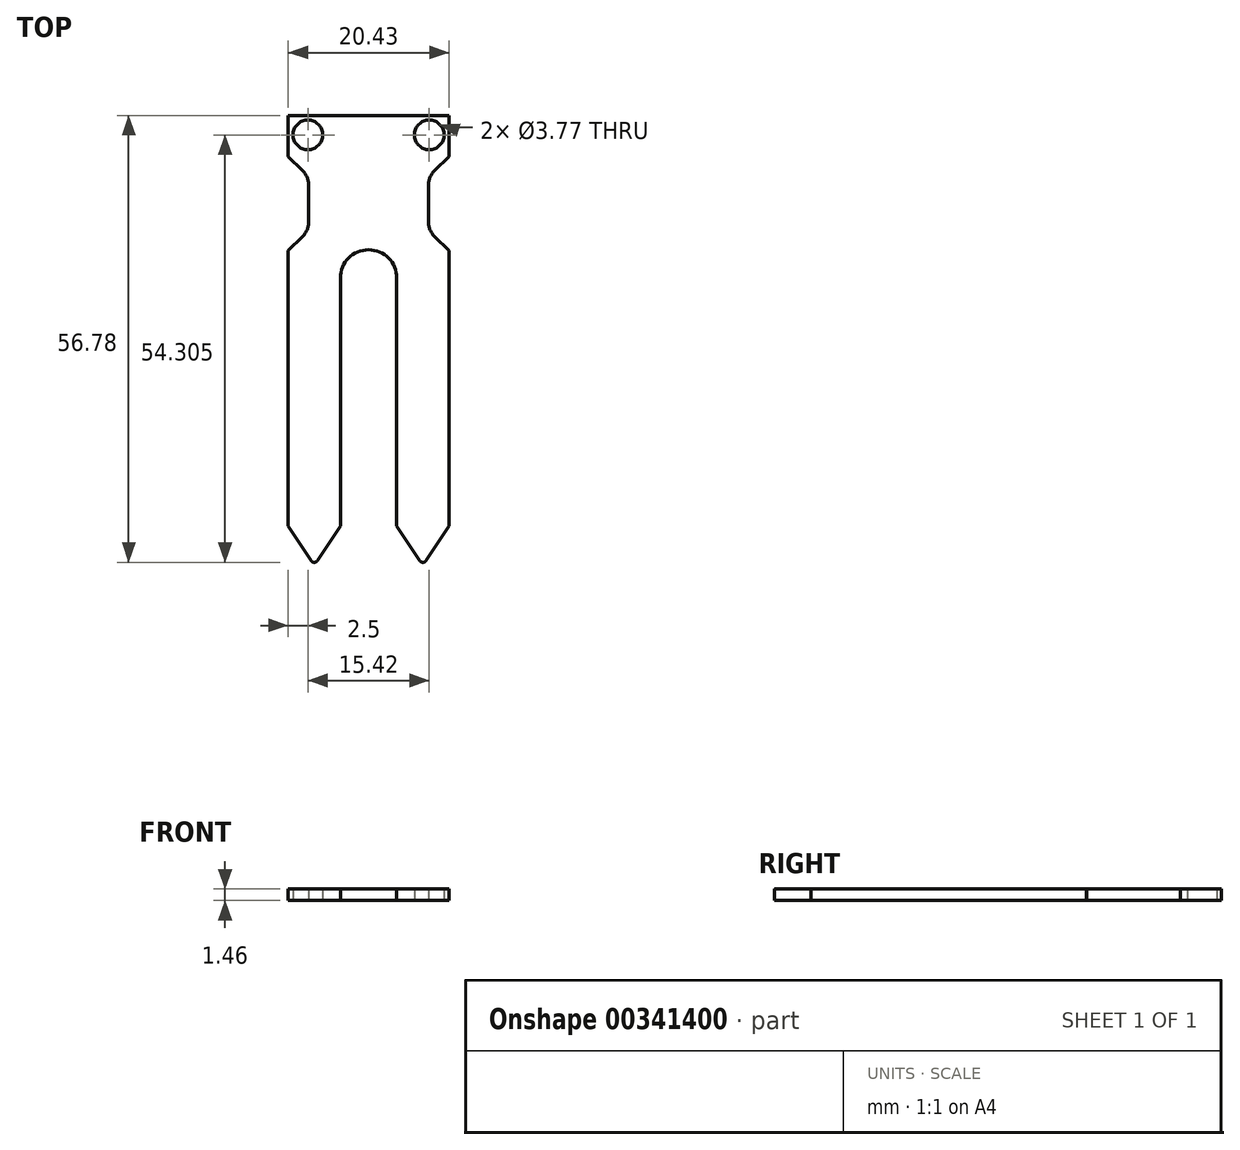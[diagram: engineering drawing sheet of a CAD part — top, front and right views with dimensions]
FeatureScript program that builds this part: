
annotation { "Feature Type Name" : "Feature", "Feature Type Description" : "" }
export const myFeature = defineFeature(function(context is Context, id is Id, definition is map)
    precondition{}
    {
        {
            var Q0;
            Q0=qCreatedBy(makeId("Top.planeOp"),FACE);
            var sketch = newSketch(context, id + "F0", { "sketchPlane" : qUnion([Q0])});
            skPoint(sketch, "E0.middle", {"position": v(0, 0) * mm});
            skLineSegment(sketch, "E1.bottom", {"start": v(-10.21, 10.33) * mm, "end": v(10.22, 10.33) * mm});
            skLineSegment(sketch, "E1.top", {"start": v(-10.22, -10.33) * mm, "end": v(10.21, -10.33) * mm, "construction": true});
            skLineSegment(sketch, "E1.left", {"start": v(-10.21, 10.33) * mm, "end": v(-10.21, -10.33) * mm});
            skLineSegment(sketch, "E1.right", {"start": v(10.21, 10.33) * mm, "end": v(10.21, -10.33) * mm});
            skArc(sketch, "E2", {"start": v(3.58, -10.33) * mm, "mid": v(0, -6.74) * mm, "end": v(-3.59, -10.33) * mm});
            skLineSegment(sketch, "E3", {"start": v(10.21, 10.33) * mm, "end": v(10.21, 5.1) * mm, "construction": true});
            skLineSegment(sketch, "E4", {"start": v(10.21, 5.1) * mm, "end": v(10.21, -6.84) * mm, "construction": true});
            skLineSegment(sketch, "E5", {"start": v(0, 0) * mm, "end": v(0, -25.8) * mm, "construction": true});
            skPoint(sketch, "E5.endSnap0", {"position": v(0, -6.74) * mm});
            skCircle(sketch, "E6", {"center": v(7.7, 7.86) * mm, "radius": 1.89 * mm});
            skCircle(sketch, "E7.MirrorC", {"center": v(-7.7, 7.86) * mm, "radius": 1.89 * mm});
            skLineSegment(sketch, "E8", {"start": v(6.9, -46.86) * mm, "end": v(6.9, -10.33) * mm, "construction": true});
            skPoint(sketch, "E9.oppositeSnap0", {"position": v(10.22, -26.08) * mm});
            skLineSegment(sketch, "E9.bottom", {"start": v(3.58, -10.33) * mm, "end": v(10.22, -10.33) * mm});
            skLineSegment(sketch, "E10", {"start": v(10.21, -10.33) * mm, "end": v(10.21, -41.83) * mm});
            skLineSegment(sketch, "E11", {"start": v(10.21, -41.83) * mm, "end": v(6.9, -46.86) * mm});
            skLineSegment(sketch, "E12.MirrorCS", {"start": v(3.58, -41.83) * mm, "end": v(6.9, -46.86) * mm});
            skLineSegment(sketch, "E13.MirrorCS", {"start": v(3.58, -10.33) * mm, "end": v(3.58, -41.83) * mm});
            skLineSegment(sketch, "E14.MirrorCS", {"start": v(-3.58, -10.33) * mm, "end": v(-3.58, -41.83) * mm});
            skLineSegment(sketch, "E15.MirrorCS", {"start": v(-3.58, -41.83) * mm, "end": v(-6.9, -46.86) * mm});
            skLineSegment(sketch, "E16.MirrorCS", {"start": v(-10.22, -41.83) * mm, "end": v(-6.9, -46.86) * mm});
            skLineSegment(sketch, "E17.MirrorCS", {"start": v(-10.21, -10.33) * mm, "end": v(-10.22, -41.83) * mm});
            skLineSegment(sketch, "E18", {"start": v(10.21, -6.84) * mm, "end": v(10.21, -4.3) * mm, "construction": true});
            skLineSegment(sketch, "E19", {"start": v(10.21, -0.87) * mm, "end": v(6.5, -0.87) * mm, "construction": true});
            skLineSegment(sketch, "E20.MirrorCS", {"start": v(10.22, 5.1) * mm, "end": v(10.22, 2.56) * mm, "construction": true});
            skPoint(sketch, "E21.endSnap0", {"position": v(8.35, -0.87) * mm});
            skLineSegment(sketch, "E22", {"start": v(10.22, 2.56) * mm, "end": v(7.6, 2.56) * mm, "construction": true});
            skLineSegment(sketch, "E23", {"start": v(10.21, 5.1) * mm, "end": v(7.6, 2.56) * mm});
            skLineSegment(sketch, "E24.MirrorCS", {"start": v(10.21, -6.84) * mm, "end": v(7.6, -4.3) * mm});
            skLineSegment(sketch, "E25", {"start": v(7.6, 2.56) * mm, "end": v(7.6, -4.3) * mm});
            skLineSegment(sketch, "E26.MirrorCS", {"start": v(-10.21, 5.1) * mm, "end": v(-7.6, 2.56) * mm});
            skLineSegment(sketch, "E27.MirrorCS", {"start": v(-7.6, 2.56) * mm, "end": v(-7.6, -4.3) * mm});
            skLineSegment(sketch, "E28.MirrorCS", {"start": v(-10.21, -6.84) * mm, "end": v(-7.6, -4.3) * mm});
            skSolve(sketch);
        }
        {
            var Q0;
            Q0=makeQuery(id+"F0.imprint","IMPRINT",FACE,{"disambiguationData":[TD([[makeQuery(id+"F0.imprint","IMPRINT",EDGE,{"derivedFrom":sQuery(id+"F0.wireOp",EDGE,"E1.bottom")}),-1.0]])]});
            var Q1;
            Q1=makeQuery(id+"F0.imprint","IMPRINT",FACE,{"disambiguationData":[TD([[makeQuery(id+"F0.imprint","IMPRINT",EDGE,{"derivedFrom":sQuery(id+"F0.wireOp",EDGE,"E9.bottom")}),-1.0]])]});
            extrude(context, id + "F1", {"entities" : qUnion([Q0, Q1]), "depth" : 1.46 * mm});
        }
        {
            var Q0;
            Q0=makeQuery(id+"F1.opExtrude","SWEPT_EDGE",EDGE,{"disambiguationData":[OSD([sQuery(id+"F0.wireOp",EDGE,"E26.MirrorCS"),sQuery(id+"F0.wireOp",EDGE,"E27.MirrorCS")])]});
            fillet(context, id + "F2", {"entities" : qUnion([Q0]), "radius" : 2.5 * mm, "tangentPropagation" : true, "allowEdgeOverflow" : false});
        }
        {
            var Q0;
            Q0=makeQuery(id+"F1.opExtrude","SWEPT_EDGE",EDGE,{"disambiguationData":[OSD([sQuery(id+"F0.wireOp",EDGE,"E27.MirrorCS"),sQuery(id+"F0.wireOp",EDGE,"E28.MirrorCS")])]});
            fillet(context, id + "F3", {"entities" : qUnion([Q0]), "radius" : 2.5 * mm, "tangentPropagation" : true, "allowEdgeOverflow" : false});
        }
        {
            var Q0;
            Q0=makeQuery(id+"F1.opExtrude","SWEPT_EDGE",EDGE,{"disambiguationData":[OSD([sQuery(id+"F0.wireOp",EDGE,"E24.MirrorCS"),sQuery(id+"F0.wireOp",EDGE,"E25")])]});
            fillet(context, id + "F4", {"entities" : qUnion([Q0]), "radius" : 2.5 * mm, "tangentPropagation" : true, "allowEdgeOverflow" : false});
        }
        {
            var Q0;
            Q0=makeQuery(id+"F1.opExtrude","SWEPT_EDGE",EDGE,{"disambiguationData":[OSD([sQuery(id+"F0.wireOp",EDGE,"E23"),sQuery(id+"F0.wireOp",EDGE,"E25")])]});
            fillet(context, id + "F5", {"entities" : qUnion([Q0]), "radius" : 2.5 * mm, "tangentPropagation" : true, "allowEdgeOverflow" : false});
        }
        {
            var Q0;
            Q0=makeQuery(id+"F1.opExtrude","SWEPT_EDGE",EDGE,{"disambiguationData":[OSD([sQuery(id+"F0.wireOp",EDGE,"E15.MirrorCS"),sQuery(id+"F0.wireOp",EDGE,"E16.MirrorCS")])]});
            var Q1;
            Q1=makeQuery(id+"F1.opExtrude","SWEPT_EDGE",EDGE,{"disambiguationData":[OSD([sQuery(id+"F0.wireOp",EDGE,"E11"),sQuery(id+"F0.wireOp",EDGE,"E12.MirrorCS")])]});
            fillet(context, id + "F6", {"entities" : qUnion([Q0, Q1]), "radius" : 0.5 * mm, "tangentPropagation" : true, "allowEdgeOverflow" : false});
        }
    });
